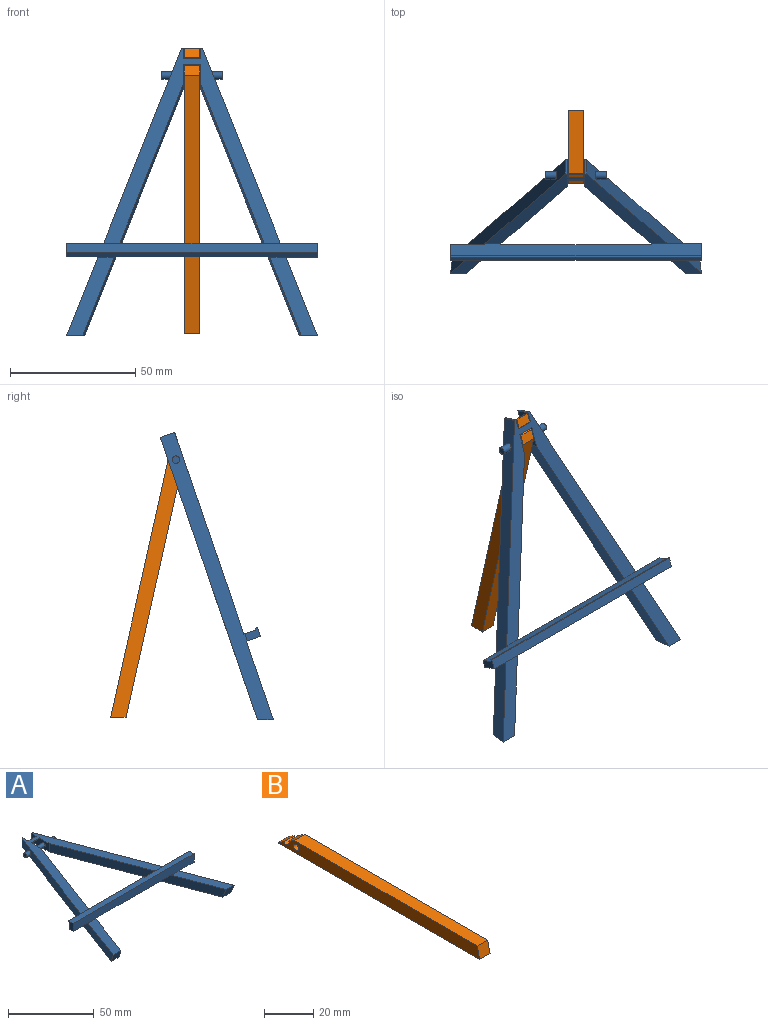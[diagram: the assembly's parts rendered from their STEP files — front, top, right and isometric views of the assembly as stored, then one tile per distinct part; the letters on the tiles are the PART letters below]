
ASSEMBLY  parts=2 mates=1
PART A: 31 faces, bbox 100.2x121.3x12.2 mm
  f0: plane 13.64x3mm, normal (0,0,-1), area 39.2mm2, adj f11,f13,f17,f25
  f1: plane 62.17x3mm, normal (0,0,-1), area 183.1mm2, adj f7,f11,f13,f23
  f2: plane 6x0.8mm, normal (0,1,0), area 4.8mm2, adj f3,f4,f8,f9
  f3: plane 118.97x45.82mm, normal (0,0,-1), area 721.5mm2, adj f2,f6,f7,f8,f9
  f4: plane 85x72.73mm, normal (0,0,1), area 1024.9mm2, adj f2,f7,f8,f9,f13,f18,f22,f23
  f5: plane 33.03x18.92mm, normal (0,0,1), area 211.9mm2, adj f6,f7,f9,f11
  f6: plane 7.2x6mm, normal (0,-0.95,-0.33), area 40.7mm2, adj f3,f5,f7,f9
  f7: plane 106.19x40.18mm, normal (-0.94,-0.35,0), area 675.9mm2, adj f1,f3,f4,f5,f6,f8,f11,f13
  f8: plane 14.84x6mm, normal (-1,0,0), area 81.1mm2, adj f2,f3,f4,f7,f18,f30
  f9: plane 121.03x45.8mm, normal (0.94,0.35,0), area 762.3mm2, adj f2,f3,f4,f5,f6,f12,f28
  f10: plane 100x3.86mm, normal (0,0,1), area 385.7mm2, adj f11,f15,f16,f17
  f11: plane 100x6mm, normal (0,-1,0), area 570.1mm2, adj f0,f1,f5,f7,f10,f12,f16,f17
  f12: plane 13.64x3mm, normal (0,0,-1), area 39.2mm2, adj f9,f11,f13,f16
  f13: plane 100x4.8mm, normal (0,1,0), area 450.6mm2, adj f0,f1,f4,f7,f12,f14,f16,f17
  f14: plane 100x0.86mm, normal (0,0.57,-0.82), area 104.6mm2, adj f13,f15,f16,f17
  f15: plane 100x0.6mm, normal (0,1,0), area 60mm2, adj f10,f14,f16,f17
  f16: plane 6x3.86mm, normal (1,0,0), area 18.8mm2, adj f10,f11,f12,f13,f14,f15
  f17: plane 5.6x3.86mm, normal (-1,0,0), area 17.6mm2, adj f0,f10,f11,f13,f14,f15
  f18: cylinder r=1.3mm len=6.8mm, axis (-1,0,0), area 27.8mm2, adj f4,f8,f24
  f19: plane 7.2x6mm, normal (0,-0.95,-0.33), area 40.7mm2, adj f20,f21,f23,f25
  f20: plane 33.03x18.92mm, normal (0,0,1), area 211.9mm2, adj f11,f19,f23,f25
  f21: plane 118.97x45.82mm, normal (0,0,-1), area 721.5mm2, adj f19,f22,f23,f24,f25
  f22: plane 6x0.8mm, normal (0,1,0), area 4.8mm2, adj f4,f21,f24,f25
  f23: plane 106.19x40.18mm, normal (0.94,-0.35,0), area 675.9mm2, adj f1,f4,f11,f13,f19,f20,f21,f24
  f24: plane 14.84x6mm, normal (1,0,0), area 81.1mm2, adj f4,f18,f21,f22,f23,f30
  f25: plane 121.27x46.04mm, normal (-0.94,0.35,0), area 763.6mm2, adj f0,f4,f11,f13,f19,f20,f21,f22
  f26: plane 3x3mm, normal (-1,0,0), area 7.1mm2, adj f27
  f27: cylinder r=1.5mm len=4.43mm, axis (-1,0,0), area 36.4mm2, adj f25,f26
  f28: cylinder r=1.5mm len=4.43mm, axis (-1,0,0), area 36.4mm2, adj f9,f29
  f29: plane 3x3mm, normal (1,0,0), area 7.1mm2, adj f28
  f30: cylinder r=1.3mm len=6.8mm, axis (1,0,0), area 55.5mm2, adj f8,f24
PART B: 11 faces, bbox 6x116.3x6 mm
  f0: plane 116.33x6mm, normal (0,0,-1), area 698mm2, adj f1,f8,f9,f10
  f1: plane 6x0.24mm, normal (0,1,0), area 1.4mm2, adj f0,f2,f9,f10
  f2: plane 6x3.31mm, normal (0,0.52,0.86), area 23.1mm2, adj f1,f3,f9,f10
  f3: cylinder r=1.5mm len=6mm, axis (-1,0,0), area 23.4mm2, adj f2,f4,f9,f10
  f4: plane 6x0.9mm, normal (0,1,0), area 5.4mm2, adj f3,f5,f9,f10
  f5: plane 6x3.49mm, normal (0,0.52,0.86), area 24.4mm2, adj f4,f6,f9,f10
  f6: plane 105.47x6mm, normal (0,0,1), area 632.8mm2, adj f5,f8,f9,f10
  f7: cylinder r=1.5mm len=6mm, axis (-1,0,0), area 56.5mm2, adj f9,f10
  f8: plane 6x6mm, normal (0,-0.98,0.21), area 36.8mm2, adj f0,f6,f9,f10
  f9: plane 116.33x6mm, normal (1,0,0), area 655.9mm2, adj f0,f1,f2,f3,f4,f5,f6,f7
  f10: plane 116.33x6mm, normal (-1,0,0), area 655.9mm2, adj f0,f1,f2,f3,f4,f5,f6,f7
PLACE A rot(axis=(1,0,0),71deg) t=(14.95,9.65,34.66)mm fixed
PLACE B rot(axis=(1,0,0),102.6deg) t=(14.95,9.65,34.66)mm
MATE revolute B.f7 <-> A.f27  axis (-1,0,0) through (14.95,9.65,34.66)mm
